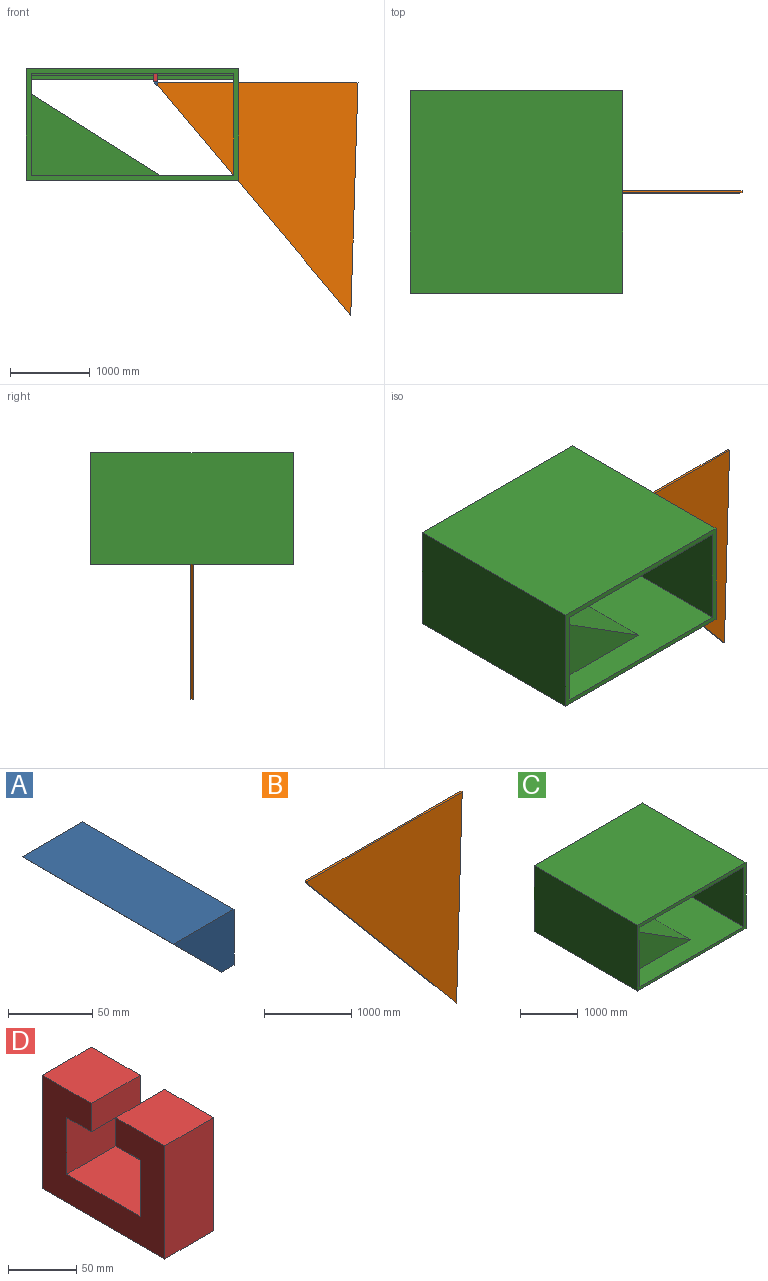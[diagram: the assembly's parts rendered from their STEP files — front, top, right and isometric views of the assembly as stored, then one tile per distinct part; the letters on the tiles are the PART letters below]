
ASSEMBLY  parts=4 mates=3
PART A: 8 faces, bbox 53.3x127x40.6 mm
  f0: plane 127x50.8mm, normal (0,0,1), area 6451.6mm2, adj f1,f3,f4,f5
  f1: plane 127x40.64mm, normal (-0.71,0,-0.71), area 7299.2mm2, adj f0,f2,f4,f5
  f2: plane 127x10.16mm, normal (0,0,-1), area 1290.3mm2, adj f1,f3,f4,f5
  f3: plane 127x40.64mm, normal (1,0,0), area 5034.6mm2, adj f0,f2,f4,f5,f6
  f4: plane 50.8x40.64mm, normal (0,-1,0), area 1238.7mm2, adj f0,f1,f2,f3
  f5: plane 50.8x40.64mm, normal (0,1,0), area 1238.7mm2, adj f0,f1,f2,f3
  f6: cylinder r=6.35mm len=12.7mm, axis (-1,0,0), area 101.3mm2, adj f3,f7
  f7: plane 12.7x12.7mm, normal (1,0,0), area 126.7mm2, adj f6
PART B: 6 faces, bbox 2510.8x25.4x2918.6 mm
  f0: plane 34.77x25.4mm, normal (-1,0,0), area 883.1mm2, adj f1,f3,f4,f5
  f1: plane 2883.86x2419.85mm, normal (-0.77,0,-0.64), area 95621.2mm2, adj f0,f2,f4,f5
  f2: plane 2918.63x90.98mm, normal (1,0,-0.03), area 74169.2mm2, adj f1,f3,f4,f5
  f3: plane 2510.83x25.4mm, normal (0,0,1), area 63775mm2, adj f0,f2,f4,f5
  f4: plane 2918.63x2510.83mm, normal (0,-1,0), area 3706152.1mm2, adj f0,f1,f2,f3
  f5: plane 2918.63x2510.83mm, normal (0,1,0), area 3706152.1mm2, adj f0,f1,f2,f3
PART C: 21 faces, bbox 2667x2540x1397 mm
  f0: plane 2540x1270mm, normal (1,0,0), area 1414835.9mm2, adj f2,f3,f4,f9,f10,f11,f12,f13
  f1: plane 2540x1270mm, normal (-1,0,0), area 3221283.9mm2, adj f2,f3,f4,f9,f10,f14,f15,f16
  f2: plane 2540x1257.3mm, normal (0,0,-1), area 3193542mm2, adj f0,f1,f10,f15
  f3: plane 2540x2540mm, normal (0,0,1), area 3586443.1mm2, adj f0,f1,f9,f10,f11,f12,f13
  f4: plane 2540x1257.3mm, normal (0,0,-1), area 3193542mm2, adj f0,f1,f9,f14
  f5: plane 2540x1397mm, normal (1,0,0), area 3548380mm2, adj f6,f8,f9,f10
  f6: plane 2667x2540mm, normal (0,0,1), area 6774180mm2, adj f5,f7,f9,f10
  f7: plane 2540x1397mm, normal (-1,0,0), area 3548380mm2, adj f6,f8,f9,f10
  f8: plane 2667x2540mm, normal (0,0,-1), area 6774180mm2, adj f5,f7,f9,f10
  f9: plane 2667x1397mm, normal (0,-1,0), area 499999mm2, adj f0,f1,f3,f4,f5,f6,f7,f8
  f10: plane 2667x1397mm, normal (0,1,0), area 499999mm2, adj f0,f1,f2,f3,f5,f6,f7,f8
  f11: plane 1778x1611.45mm, normal (0.53,0,0.85), area 3387090mm2, adj f0,f3,f12,f13
  f12: plane 1611.45x1016mm, normal (0,-1,0), area 818616.3mm2, adj f0,f3,f11
  f13: plane 1611.45x1016mm, normal (0,1,0), area 818616.3mm2, adj f0,f3,f11
  f14: plane 2540x25.4mm, normal (0,-1,0), area 64516mm2, adj f0,f1,f4,f16
  f15: plane 2540x25.4mm, normal (0,1,0), area 64516mm2, adj f0,f1,f2,f17
  f16: plane 2540x25.4mm, normal (0,0,1), area 64516mm2, adj f0,f1,f14,f19
  f17: plane 2540x25.4mm, normal (0,0,1), area 64516mm2, adj f0,f1,f15,f20
  f18: plane 2540x76.2mm, normal (0,0,-1), area 193548mm2, adj f0,f1,f19,f20
  f19: plane 2540x50.8mm, normal (0,-1,0), area 129032mm2, adj f0,f1,f16,f18
  f20: plane 2540x50.8mm, normal (0,1,0), area 129032mm2, adj f0,f1,f17,f18
PART D: 14 faces, bbox 50.8x127x101.6 mm
  f0: plane 50.8x50.8mm, normal (0,0,1), area 2580.6mm2, adj f1,f2,f5,f7
  f1: plane 127x101.6mm, normal (1,0,0), area 8387.1mm2, adj f0,f3,f4,f5,f6,f7,f8,f9
  f2: plane 127x101.6mm, normal (-1,0,0), area 8387.1mm2, adj f0,f3,f4,f5,f6,f7,f8,f9
  f3: plane 50.8x50.8mm, normal (0,0,1), area 2580.6mm2, adj f1,f2,f6,f13
  f4: plane 127x50.8mm, normal (0,0,-1), area 6451.6mm2, adj f1,f2,f5,f6
  f5: plane 101.6x50.8mm, normal (0,-1,0), area 5161.3mm2, adj f0,f1,f2,f4
  f6: plane 101.6x50.8mm, normal (0,1,0), area 5161.3mm2, adj f1,f2,f3,f4
  f7: plane 50.8x25.4mm, normal (0,1,0), area 1290.3mm2, adj f0,f1,f2,f8
  f8: plane 50.8x25.4mm, normal (0,0,-1), area 1290.3mm2, adj f1,f2,f7,f9
  f9: plane 50.8x50.8mm, normal (0,1,0), area 2580.6mm2, adj f1,f2,f8,f10
  f10: plane 76.2x50.8mm, normal (0,0,1), area 3871mm2, adj f1,f2,f9,f11
  f11: plane 50.8x50.8mm, normal (0,-1,0), area 2580.6mm2, adj f1,f2,f10,f12
  f12: plane 50.8x25.4mm, normal (0,0,-1), area 1290.3mm2, adj f1,f2,f11,f13
  f13: plane 50.8x25.4mm, normal (0,-1,0), area 1290.3mm2, adj f1,f2,f3,f12
PLACE A t=(292.1,0,584.71)mm
PLACE B t=(246.47,0,504.18)mm
PLACE C at identity fixed
PLACE D t=(292.1,0,584.2)mm
MATE fastened B.f0 <-> A.f6  axis (-1,0,0) through (320.04,0,508.51)mm
MATE fastened C.f18 <-> D.f10  axis (0,0,-1) through (292.1,0,558.8)mm
MATE fastened D.f4 <-> A.f0  axis (0,0,-1) through (292.1,0,533.4)mm
